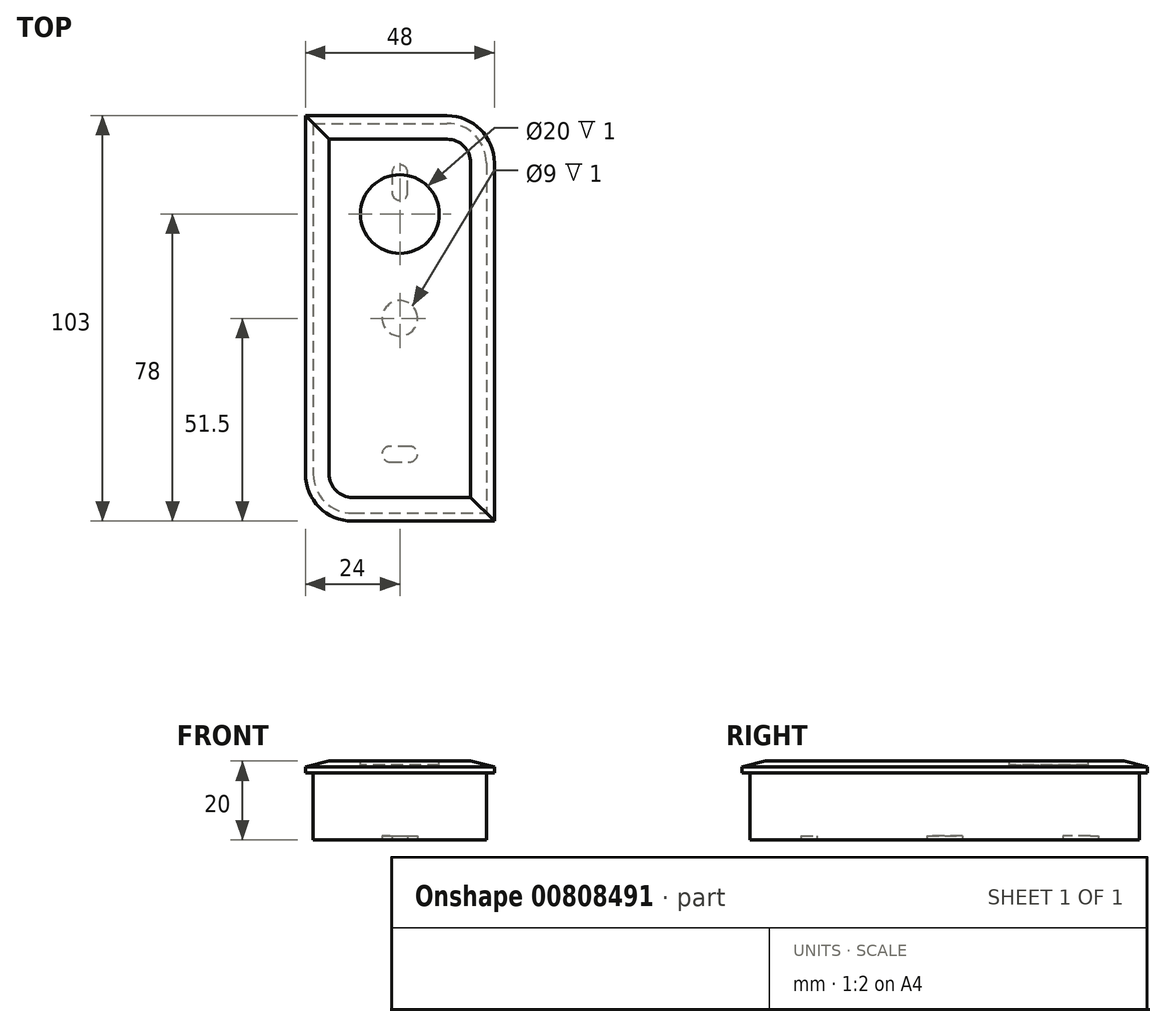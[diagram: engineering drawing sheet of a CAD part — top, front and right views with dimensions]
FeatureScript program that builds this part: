
annotation { "Feature Type Name" : "Feature", "Feature Type Description" : "" }
export const myFeature = defineFeature(function(context is Context, id is Id, definition is map)
    precondition{}
    {
        {
            var Q0;
            Q0=qCreatedBy(makeId("Top.planeOp"),FACE);
            var sketch = newSketch(context, id + "F0", { "sketchPlane" : qUnion([Q0])});
            skLineSegment(sketch, "E0.bottom", {"start": v(-22, 49.5) * mm, "end": v(22, 49.5) * mm});
            skLineSegment(sketch, "E0.top", {"start": v(-22, -49.5) * mm, "end": v(22, -49.5) * mm});
            skLineSegment(sketch, "E0.left", {"start": v(-22, 49.5) * mm, "end": v(-22, -49.5) * mm});
            skLineSegment(sketch, "E0.right", {"start": v(22, 49.5) * mm, "end": v(22, -49.5) * mm});
            skPoint(sketch, "E0.middle", {"position": v(0, 0) * mm});
            skSolve(sketch);
        }
        {
            var Q0;
            Q0 = qSketchRegion(id + "F0", true);
            extrude(context, id + "F1", {"entities" : qUnion([Q0]), "depth" : 20 * mm, "offsetDistance" : 25 * mm});
        }
        {
            var Q0;
            Q0=makeQuery(id+"F1.opExtrude","SWEPT_EDGE",EDGE,{"disambiguationData":[OSD([sQuery(id+"F0.wireOp",EDGE,"E0.bottom"),sQuery(id+"F0.wireOp",EDGE,"E0.right")])]});
            var Q1;
            Q1=makeQuery(id+"F1.opExtrude","SWEPT_EDGE",EDGE,{"disambiguationData":[OSD([sQuery(id+"F0.wireOp",EDGE,"E0.top"),sQuery(id+"F0.wireOp",EDGE,"E0.left")])]});
            fillet(context, id + "F2", {"entities" : qUnion([Q0, Q1]), "radius" : 10 * mm, "tangentPropagation" : true, "allowEdgeOverflow" : false});
        }
        {
            var Q0;
            Q0=makeQuery(id+"F1.opExtrude","CAP_FACE",FACE,{"disambiguationData":[OSD([sQuery(id+"F0.wireOp",EDGE,"E0.bottom"),sQuery(id+"F0.wireOp",EDGE,"E0.top"),sQuery(id+"F0.wireOp",EDGE,"E0.left"),sQuery(id+"F0.wireOp",EDGE,"E0.right")])],"isStart":false});
            var sketch = newSketch(context, id + "F3", { "sketchPlane" : qUnion([Q0])});
            skLineSegment(sketch, "E1.0", {"start": v(12, 51.5) * mm, "end": v(-24, 51.5) * mm});
            skArc(sketch, "E1.1", {"start": v(-24, -39.5) * mm, "mid": v(-20.49, -47.99) * mm, "end": v(-12, -51.5) * mm});
            skLineSegment(sketch, "E1.2", {"start": v(-12, -51.5) * mm, "end": v(24, -51.5) * mm});
            skLineSegment(sketch, "E1.3", {"start": v(-24, 51.5) * mm, "end": v(-24, -39.5) * mm});
            skLineSegment(sketch, "E1.4", {"start": v(24, -51.5) * mm, "end": v(24, 39.5) * mm});
            skArc(sketch, "E1.5", {"start": v(24, 39.5) * mm, "mid": v(20.49, 47.99) * mm, "end": v(12, 51.5) * mm});
            skSolve(sketch);
        }
        {
            var Q0;
            Q0 = qSketchRegion(id + "F3", true);
            extrude(context, id + "F4", {"entities" : qUnion([Q0]), "operationType" : NewBodyOperationType.ADD, "oppositeDirection" : true, "depth" : 3 * mm, "offsetDistance" : 25 * mm});
        }
        {
            var Q0;
            Q0=makeQuery(id+"F4.boolean.opBoolean","MERGE",FACE,{"derivedFrom":[makeQuery(id+"F1.opExtrude","CAP_FACE",FACE,{"disambiguationData":[OSD([sQuery(id+"F0.wireOp",EDGE,"E0.bottom"),sQuery(id+"F0.wireOp",EDGE,"E0.top"),sQuery(id+"F0.wireOp",EDGE,"E0.left"),sQuery(id+"F0.wireOp",EDGE,"E0.right")])],"isStart":false}),makeQuery(id+"F4.opExtrude","CAP_FACE",FACE,{"disambiguationData":[OSD([sQuery(id+"F3.wireOp",EDGE,"E1.0"),sQuery(id+"F3.wireOp",EDGE,"E1.1"),sQuery(id+"F3.wireOp",EDGE,"E1.2"),sQuery(id+"F3.wireOp",EDGE,"E1.3"),sQuery(id+"F3.wireOp",EDGE,"E1.4"),sQuery(id+"F3.wireOp",EDGE,"E1.5")])],"isStart":true})]});
            chamfer(context, id + "F5", {"entities" : qUnion([Q0]), "chamferType" : ChamferType.TWO_OFFSETS, "width1" : 6 * mm, "oppositeDirection" : false, "width2" : 1.5 * mm, "tangentPropagation" : true});
        }
        {
            var Q0;
            Q0=makeQuery(id+"F4.boolean.opBoolean","MERGE",FACE,{"derivedFrom":[makeQuery(id+"F1.opExtrude","CAP_FACE",FACE,{"disambiguationData":[OSD([sQuery(id+"F0.wireOp",EDGE,"E0.bottom"),sQuery(id+"F0.wireOp",EDGE,"E0.top"),sQuery(id+"F0.wireOp",EDGE,"E0.left"),sQuery(id+"F0.wireOp",EDGE,"E0.right")])],"isStart":false}),makeQuery(id+"F4.opExtrude","CAP_FACE",FACE,{"disambiguationData":[OSD([sQuery(id+"F3.wireOp",EDGE,"E1.0"),sQuery(id+"F3.wireOp",EDGE,"E1.1"),sQuery(id+"F3.wireOp",EDGE,"E1.2"),sQuery(id+"F3.wireOp",EDGE,"E1.3"),sQuery(id+"F3.wireOp",EDGE,"E1.4"),sQuery(id+"F3.wireOp",EDGE,"E1.5")])],"isStart":true})]});
            var sketch = newSketch(context, id + "F6", { "sketchPlane" : qUnion([Q0])});
            skCircle(sketch, "E2", {"center": v(0, 26.5) * mm, "radius": 10 * mm});
            skSolve(sketch);
        }
        {
            var Q0;
            Q0 = qSketchRegion(id + "F6", true);
            extrude(context, id + "F7", {"entities" : qUnion([Q0]), "operationType" : NewBodyOperationType.REMOVE, "oppositeDirection" : true, "depth" : 1 * mm, "offsetDistance" : 25 * mm});
        }
        {
            var Q0;
            Q0=makeQuery(id+"F1.opExtrude","CAP_FACE",FACE,{"disambiguationData":[OSD([sQuery(id+"F0.wireOp",EDGE,"E0.bottom"),sQuery(id+"F0.wireOp",EDGE,"E0.top"),sQuery(id+"F0.wireOp",EDGE,"E0.left"),sQuery(id+"F0.wireOp",EDGE,"E0.right")])],"isStart":true});
            var sketch = newSketch(context, id + "F8", { "sketchPlane" : qUnion([Q0])});
            skCircle(sketch, "E3", {"center": v(0, 0) * mm, "radius": 4.5 * mm});
            skLineSegment(sketch, "E4", {"start": v(-2, -37) * mm, "end": v(-2, -32) * mm});
            skLineSegment(sketch, "E5", {"start": v(2, -32) * mm, "end": v(2, -37) * mm});
            skArc(sketch, "E6", {"start": v(-2, -37) * mm, "mid": v(0, -39) * mm, "end": v(2, -37) * mm});
            skArc(sketch, "E7", {"start": v(2, -32) * mm, "mid": v(0, -30) * mm, "end": v(-2, -32) * mm});
            skLineSegment(sketch, "E8", {"start": v(0, -32) * mm, "end": v(0, -37) * mm, "construction": true});
            skLineSegment(sketch, "E9", {"start": v(-2, -34.5) * mm, "end": v(2, -34.5) * mm, "construction": true});
            skPoint(sketch, "E10", {"position": v(0, -34.5) * mm});
            skLineSegment(sketch, "E11", {"start": v(-2.5, 36.5) * mm, "end": v(2.5, 36.5) * mm});
            skLineSegment(sketch, "E12", {"start": v(2.5, 32.5) * mm, "end": v(-2.5, 32.5) * mm});
            skArc(sketch, "E13", {"start": v(-2.5, 36.5) * mm, "mid": v(-4.5, 34.5) * mm, "end": v(-2.5, 32.5) * mm});
            skArc(sketch, "E14", {"start": v(2.5, 32.5) * mm, "mid": v(4.5, 34.5) * mm, "end": v(2.5, 36.5) * mm});
            skLineSegment(sketch, "E15", {"start": v(2.5, 34.5) * mm, "end": v(-2.5, 34.5) * mm, "construction": true});
            skLineSegment(sketch, "E16", {"start": v(0, 36.5) * mm, "end": v(0, 32.5) * mm, "construction": true});
            skPoint(sketch, "E17", {"position": v(0, 34.5) * mm});
            skSolve(sketch);
        }
        {
            var Q0;
            Q0 = qSketchRegion(id + "F8", true);
            extrude(context, id + "F9", {"entities" : qUnion([Q0]), "operationType" : NewBodyOperationType.REMOVE, "oppositeDirection" : true, "depth" : 1 * mm, "offsetDistance" : 25 * mm});
        }
    });
